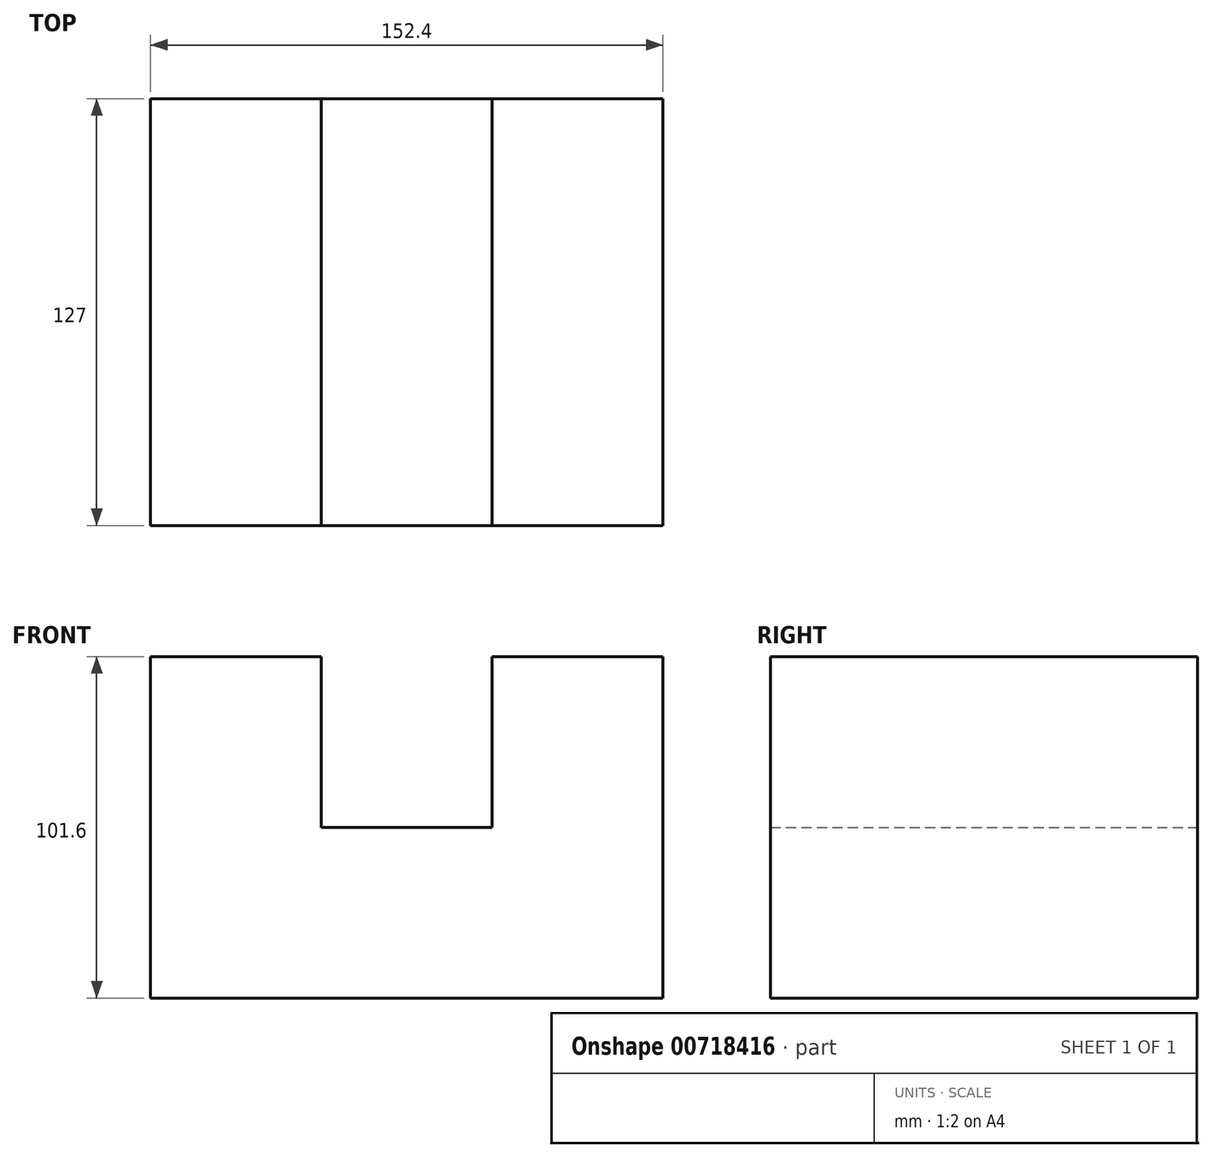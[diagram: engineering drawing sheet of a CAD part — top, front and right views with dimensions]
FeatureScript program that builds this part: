
annotation { "Feature Type Name" : "Feature", "Feature Type Description" : "" }
export const myFeature = defineFeature(function(context is Context, id is Id, definition is map)
    precondition{}
    {
        {
            var Q0;
            Q0=qCreatedBy(makeId("Front.planeOp"),FACE);
            var sketch = newSketch(context, id + "F0", { "sketchPlane" : qUnion([Q0])});
            skLineSegment(sketch, "E0", {"start": v(-90.08, -60.88) * mm, "end": v(62.32, -60.88) * mm});
            skLineSegment(sketch, "E1", {"start": v(62.32, -60.88) * mm, "end": v(62.32, 40.72) * mm});
            skLineSegment(sketch, "E2", {"start": v(62.32, 40.72) * mm, "end": v(11.52, 40.72) * mm});
            skLineSegment(sketch, "E3", {"start": v(11.52, 40.72) * mm, "end": v(11.52, -10.08) * mm});
            skLineSegment(sketch, "E4", {"start": v(11.52, -10.08) * mm, "end": v(-39.28, -10.08) * mm});
            skLineSegment(sketch, "E5", {"start": v(-39.28, -10.08) * mm, "end": v(-39.28, 40.72) * mm});
            skLineSegment(sketch, "E6", {"start": v(-39.28, 40.72) * mm, "end": v(-90.08, 40.72) * mm});
            skLineSegment(sketch, "E7", {"start": v(-90.08, 40.72) * mm, "end": v(-90.08, -60.88) * mm});
            skSolve(sketch);
        }
        {
            var Q0;
            Q0=makeQuery(id+"F0.imprint","IMPRINT",FACE,{"disambiguationData":[TD([[makeQuery(id+"F0.imprint","IMPRINT",EDGE,{"derivedFrom":sQuery(id+"F0.wireOp",EDGE,"E0")}),1.0]])]});
            extrude(context, id + "F1", {"entities" : qUnion([Q0]), "depth" : 127 * mm, "offsetDistance" : 25.4 * mm});
        }
    });
